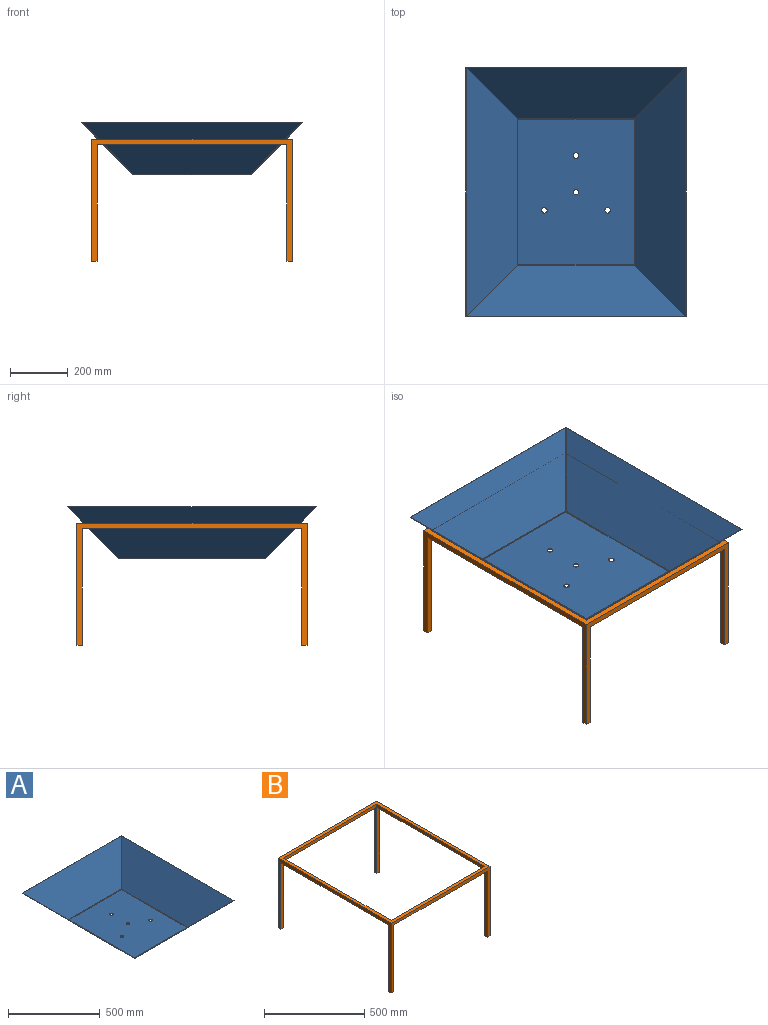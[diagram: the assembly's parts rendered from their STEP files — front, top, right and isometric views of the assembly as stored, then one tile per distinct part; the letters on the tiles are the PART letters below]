
ASSEMBLY  parts=2 mates=1
PART A: 50 faces, bbox 767.2x868.8x180.9 mm
  f0: cylinder r=9.53mm len=19.05mm, axis (0,0,1), area 112.5mm2, adj f4,f5
  f1: cylinder r=9.53mm len=19.05mm, axis (0,0,1), area 112.5mm2, adj f4,f5
  f2: cylinder r=9.53mm len=19.05mm, axis (0,0,1), area 112.5mm2, adj f4,f5
  f3: cylinder r=9.53mm len=19.05mm, axis (0,0,1), area 112.5mm2, adj f4,f5
  f4: plane 505.48x403.88mm, normal (0,0,-1), area 203008.6mm2, adj f0,f1,f2,f3,f15,f26,f37,f48
  f5: plane 505.48x403.88mm, normal (0,0,1), area 203008.6mm2, adj f0,f1,f2,f3,f16,f27,f38,f49
  f6: plane 1.74x1.33mm, normal (0,0.71,-0.71), area 3.3mm2, adj f7,f11,f12,f13
  f7: plane 179.49x179.49mm, normal (-0.82,0.41,-0.41), area 580mm2, adj f6,f10,f11,f12
  f8: plane 1.74x1.33mm, normal (0,0.71,-0.71), area 3.3mm2, adj f9,f11,f12,f14
  f9: plane 179.49x179.49mm, normal (0.82,0.41,-0.41), area 580mm2, adj f8,f10,f11,f12
  f10: plane 763.68x1.33mm, normal (0,-0.71,0.71), area 1435.4mm2, adj f7,f9,f11,f12
  f11: plane 763.68x178.16mm, normal (0,-0.71,-0.71), area 147526.4mm2, adj f6,f7,f8,f9,f10,f15
  f12: plane 763.68x178.16mm, normal (0,0.71,0.71), area 147526.4mm2, adj f6,f7,f8,f9,f10,f16
  f13: plane 3.48x2.77mm, normal (-1,0,0), area 5.9mm2, adj f6,f15,f16,f47
  f14: plane 3.48x2.77mm, normal (1,0,0), area 5.9mm2, adj f8,f15,f16,f35
  f15: cylinder r=4.93mm len=403.88mm, axis (-1,0,0), area 1563mm2, adj f4,f11,f13,f14
  f16: cylinder r=3.05mm len=403.88mm, axis (-1,0,0), area 966.8mm2, adj f5,f12,f13,f14
  f17: plane 1.74x1.33mm, normal (0,-0.71,-0.71), area 3.3mm2, adj f18,f22,f23,f24
  f18: plane 179.49x179.49mm, normal (0.82,-0.41,-0.41), area 580mm2, adj f17,f21,f22,f23
  f19: plane 1.74x1.33mm, normal (0,-0.71,-0.71), area 3.3mm2, adj f20,f22,f23,f25
  f20: plane 179.49x179.49mm, normal (-0.82,-0.41,-0.41), area 580mm2, adj f19,f21,f22,f23
  f21: plane 763.68x1.33mm, normal (0,0.71,0.71), area 1435.4mm2, adj f18,f20,f22,f23
  f22: plane 763.68x178.16mm, normal (0,0.71,-0.71), area 147526.4mm2, adj f17,f18,f19,f20,f21,f26
  f23: plane 763.68x178.16mm, normal (0,-0.71,0.71), area 147526.4mm2, adj f17,f18,f19,f20,f21,f27
  f24: plane 3.48x2.77mm, normal (1,0,0), area 5.9mm2, adj f17,f26,f27,f36
  f25: plane 3.48x2.77mm, normal (-1,0,0), area 5.9mm2, adj f19,f26,f27,f46
  f26: cylinder r=4.93mm len=403.88mm, axis (1,0,0), area 1563mm2, adj f4,f22,f24,f25
  f27: cylinder r=3.05mm len=403.88mm, axis (1,0,0), area 966.8mm2, adj f5,f23,f24,f25
  f28: plane 1.74x1.33mm, normal (-0.71,0,-0.71), area 3.3mm2, adj f29,f33,f34,f35
  f29: plane 179.49x179.49mm, normal (-0.41,-0.82,-0.41), area 580mm2, adj f28,f32,f33,f34
  f30: plane 1.74x1.33mm, normal (-0.71,0,-0.71), area 3.3mm2, adj f31,f33,f34,f36
  f31: plane 179.49x179.49mm, normal (-0.41,0.82,-0.41), area 580mm2, adj f30,f32,f33,f34
  f32: plane 865.28x1.33mm, normal (0.71,0,0.71), area 1626.4mm2, adj f29,f31,f33,f34
  f33: plane 865.28x178.16mm, normal (0.71,0,-0.71), area 173125.5mm2, adj f28,f29,f30,f31,f32,f37
  f34: plane 865.28x178.16mm, normal (-0.71,0,0.71), area 173125.5mm2, adj f28,f29,f30,f31,f32,f38
  f35: plane 3.48x2.77mm, normal (0,-1,0), area 5.9mm2, adj f14,f28,f37,f38
  f36: plane 3.48x2.77mm, normal (0,1,0), area 5.9mm2, adj f24,f30,f37,f38
  f37: cylinder r=4.93mm len=505.48mm, axis (0,-1,0), area 1956.3mm2, adj f4,f33,f35,f36
  f38: cylinder r=3.05mm len=505.48mm, axis (0,-1,0), area 1210.1mm2, adj f5,f34,f35,f36
  f39: plane 1.74x1.33mm, normal (0.71,0,-0.71), area 3.3mm2, adj f40,f44,f45,f46
  f40: plane 179.49x179.49mm, normal (0.41,0.82,-0.41), area 580mm2, adj f39,f43,f44,f45
  f41: plane 1.74x1.33mm, normal (0.71,0,-0.71), area 3.3mm2, adj f42,f44,f45,f47
  f42: plane 179.49x179.49mm, normal (0.41,-0.82,-0.41), area 580mm2, adj f41,f43,f44,f45
  f43: plane 865.28x1.33mm, normal (-0.71,0,0.71), area 1626.4mm2, adj f40,f42,f44,f45
  f44: plane 865.28x178.16mm, normal (-0.71,0,-0.71), area 173125.5mm2, adj f39,f40,f41,f42,f43,f48
  f45: plane 865.28x178.16mm, normal (0.71,0,0.71), area 173125.5mm2, adj f39,f40,f41,f42,f43,f49
  f46: plane 3.48x2.77mm, normal (0,1,0), area 5.9mm2, adj f25,f39,f48,f49
  f47: plane 3.48x2.77mm, normal (0,-1,0), area 5.9mm2, adj f13,f41,f48,f49
  f48: cylinder r=4.93mm len=505.48mm, axis (0,1,0), area 1956.3mm2, adj f4,f44,f46,f47
  f49: cylinder r=3.05mm len=505.48mm, axis (0,1,0), area 1210.1mm2, adj f5,f45,f46,f47
PART B: 25 faces, bbox 698.5x800.1x425.5 mm
  f0: plane 660.4x19.05mm, normal (0,0,-1), area 12580.6mm2, adj f3,f9,f19,f23
  f1: plane 762x19.05mm, normal (0,0,-1), area 14516.1mm2, adj f6,f10,f14,f20
  f2: plane 660.4x19.05mm, normal (0,0,-1), area 12580.6mm2, adj f5,f7,f13,f16
  f3: plane 660.4x19.05mm, normal (0,-1,0), area 12580.6mm2, adj f0,f4,f10,f12
  f4: plane 762x19.05mm, normal (-1,0,0), area 14516.1mm2, adj f3,f5,f11,f12
  f5: plane 660.4x19.05mm, normal (0,1,0), area 12580.6mm2, adj f2,f4,f10,f12
  f6: plane 800.1x425.45mm, normal (-1,0,0), area 30725.7mm2, adj f1,f7,f9,f12,f14,f15,f20,f21
  f7: plane 698.5x425.45mm, normal (0,-1,0), area 28790.3mm2, adj f2,f6,f8,f12,f13,f15,f16,f18
  f8: plane 800.1x425.45mm, normal (1,0,0), area 30725.7mm2, adj f7,f9,f11,f12,f17,f18,f22,f24
  f9: plane 698.5x425.45mm, normal (0,1,0), area 28790.3mm2, adj f0,f6,f8,f12,f19,f21,f23,f24
  f10: plane 762x19.05mm, normal (1,0,0), area 14516.1mm2, adj f1,f3,f5,f12
  f11: plane 762x19.05mm, normal (0,0,-1), area 14516.1mm2, adj f4,f8,f17,f22
  f12: plane 800.1x698.5mm, normal (0,0,1), area 55645mm2, adj f3,f4,f5,f6,f7,f8,f9,f10
  f13: plane 406.4x19.05mm, normal (1,0,0), area 7741.9mm2, adj f2,f7,f14,f15
  f14: plane 406.4x19.05mm, normal (0,1,0), area 7741.9mm2, adj f1,f6,f13,f15
  f15: plane 19.05x19.05mm, normal (0,0,-1), area 362.9mm2, adj f6,f7,f13,f14
  f16: plane 406.4x19.05mm, normal (-1,0,0), area 7741.9mm2, adj f2,f7,f17,f18
  f17: plane 406.4x19.05mm, normal (0,1,0), area 7741.9mm2, adj f8,f11,f16,f18
  f18: plane 19.05x19.05mm, normal (0,0,-1), area 362.9mm2, adj f7,f8,f16,f17
  f19: plane 406.4x19.05mm, normal (1,0,0), area 7741.9mm2, adj f0,f9,f20,f21
  f20: plane 406.4x19.05mm, normal (0,-1,0), area 7741.9mm2, adj f1,f6,f19,f21
  f21: plane 19.05x19.05mm, normal (0,0,-1), area 362.9mm2, adj f6,f9,f19,f20
  f22: plane 406.4x19.05mm, normal (0,-1,0), area 7741.9mm2, adj f8,f11,f23,f24
  f23: plane 406.4x19.05mm, normal (-1,0,0), area 7741.9mm2, adj f0,f9,f22,f24
  f24: plane 19.05x19.05mm, normal (0,0,-1), area 362.9mm2, adj f8,f9,f22,f23
PLACE A at identity
PLACE B t=(0,0,123.5)mm
MATE parallel B.f12 <-> A.f3  axis (0,0,1) through (-330.2,-381,123.5)mm
